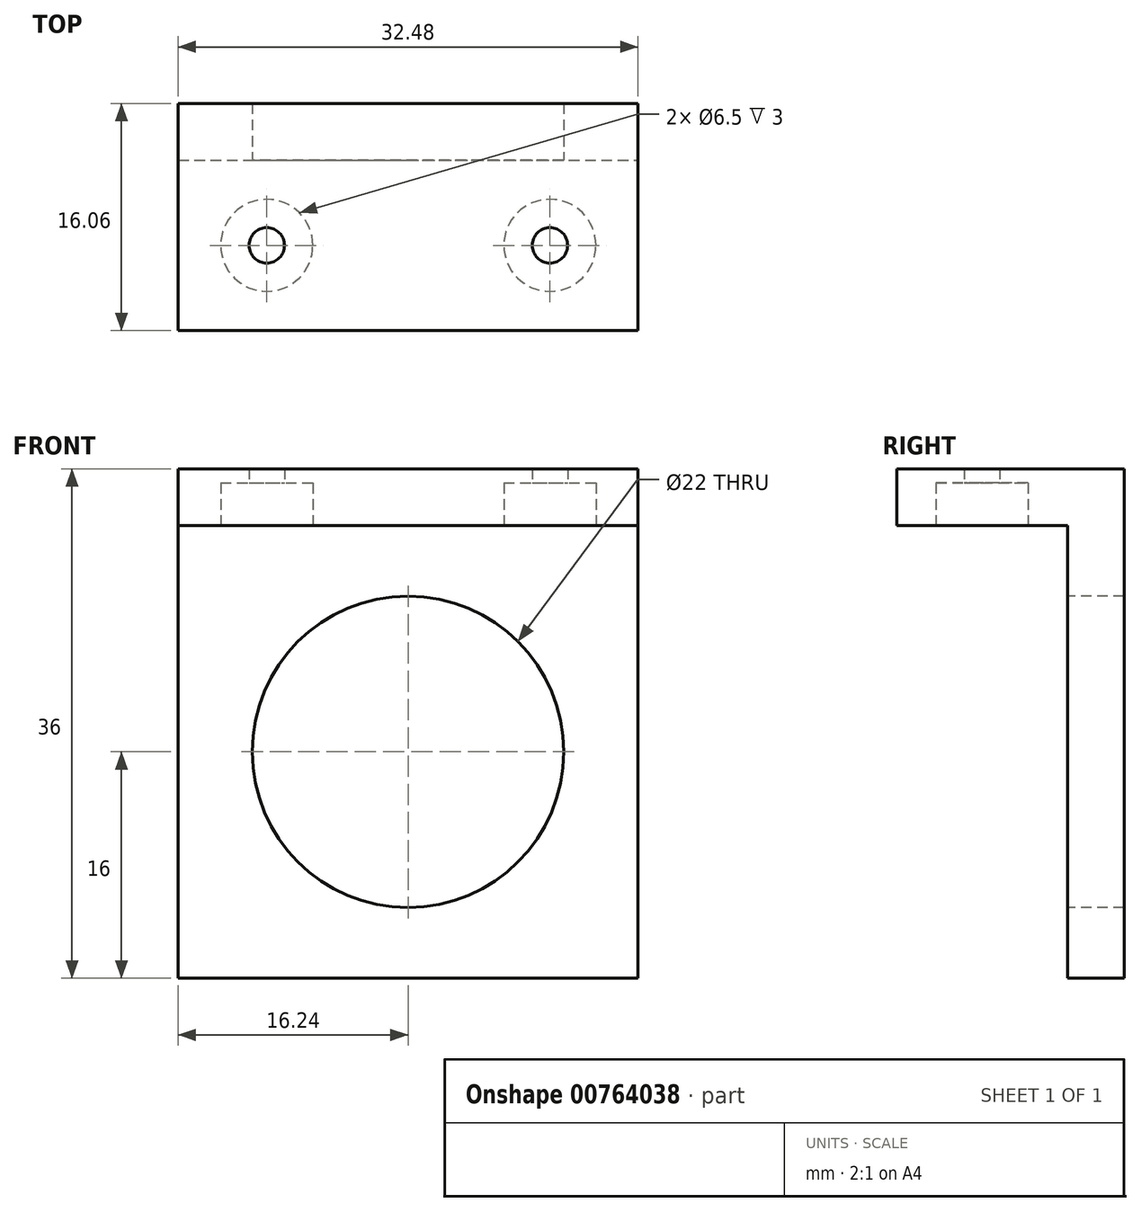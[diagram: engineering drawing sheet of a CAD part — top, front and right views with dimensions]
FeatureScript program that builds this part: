
annotation { "Feature Type Name" : "Feature", "Feature Type Description" : "" }
export const myFeature = defineFeature(function(context is Context, id is Id, definition is map)
    precondition{}
    {
        {
            var Q0;
            Q0=qCreatedBy(makeId("Top.planeOp"),FACE);
            var sketch = newSketch(context, id + "F0", { "sketchPlane" : qUnion([Q0])});
            skLineSegment(sketch, "E0.bottom", {"start": v(-16.24, 6.03) * mm, "end": v(16.24, 6.03) * mm});
            skLineSegment(sketch, "E0.top", {"start": v(-16.24, -6.03) * mm, "end": v(16.24, -6.03) * mm});
            skLineSegment(sketch, "E0.left", {"start": v(-16.24, 6.03) * mm, "end": v(-16.24, -6.03) * mm});
            skLineSegment(sketch, "E0.right", {"start": v(16.24, 6.03) * mm, "end": v(16.24, -6.03) * mm});
            skPoint(sketch, "E0.middle", {"position": v(0, 0) * mm});
            skPoint(sketch, "E1", {"position": v(-9.98, 0) * mm});
            skPoint(sketch, "E2", {"position": v(10.02, 0) * mm});
            skSolve(sketch);
        }
        {
            var Q0;
            Q0=makeQuery(id+"F0.imprint","IMPRINT",FACE,{"disambiguationData":[TD([[makeQuery(id+"F0.imprint","IMPRINT",EDGE,{"derivedFrom":sQuery(id+"F0.wireOp",EDGE,"E0.bottom")}),-1.0]])]});
            extrude(context, id + "F1", {"entities" : qUnion([Q0]), "depth" : 4 * mm, "offsetDistance" : 25 * mm});
        }
        {
            var Q0;
            Q0=sQuery(id+"F0.wireOp",VERTEX,"E2");
            var Q1;
            Q1=sQuery(id+"F0.wireOp",VERTEX,"E1");
            var Q2;
            Q2=makeQuery(id+"F1.opExtrude","SWEPT_BODY",BODY,{"disambiguationData":[OSD([sQuery(id+"F0.wireOp",EDGE,"E0.bottom"),sQuery(id+"F0.wireOp",EDGE,"E0.top"),sQuery(id+"F0.wireOp",EDGE,"E0.left"),sQuery(id+"F0.wireOp",EDGE,"E0.right")])]});
            hole(context, id + "F2", {"style" : HoleStyle.C_BORE, "endStyle" : HoleEndStyle.BLIND, "oppositeDirection" : true, "standardTappedOrClearance" : lookupTablePath({ "standard" : "ISO", "engagement" : "75%", "pitch" : "0.5 mm", "size" : "M3", "type" : "Tapped" }), "standardBlindInLast" : lookupTablePath({ "standard" : "ISO", "engagement" : "75%", "pitch" : "0.5 mm", "size" : "M3", "type" : "Tapped" }), "holeDiameter" : 2.5 * mm, "cBoreDiameter" : 6.5 * mm, "cBoreDepth" : 3 * mm, "majorDiameter" : 3 * mm, "showTappedDepth" : true, "holeDepth" : 13.5 * mm, "isTappedThrough" : true, "tappedDepth" : 12 * mm, "tapClearance" : 3, "locations" : qUnion([Q0, Q1]), "scope" : qUnion([Q2])});
        }
        {
            var Q0;
            Q0=makeQuery(id+"F1.opExtrude","SWEPT_FACE",FACE,{"disambiguationData":[OSD([sQuery(id+"F0.wireOp",EDGE,"E0.bottom")])]});
            var sketch = newSketch(context, id + "F3", { "sketchPlane" : qUnion([Q0])});
            skLineSegment(sketch, "E3.bottom", {"start": v(-16.24, 4) * mm, "end": v(16.24, 4) * mm});
            skLineSegment(sketch, "E3.top", {"start": v(-16.24, -32) * mm, "end": v(16.24, -32) * mm});
            skLineSegment(sketch, "E3.left", {"start": v(-16.24, 4) * mm, "end": v(-16.24, -32) * mm});
            skLineSegment(sketch, "E3.right", {"start": v(16.24, 4) * mm, "end": v(16.24, -32) * mm});
            skPoint(sketch, "E4", {"position": v(0, -16) * mm});
            skCircle(sketch, "E5", {"center": v(0, -16) * mm, "radius": 11 * mm});
            skSolve(sketch);
        }
        {
            var Q0;
            {var subQ0=sQuery(id+"F3.wireOp",EDGE,"E3.bottom");Q0=makeQuery(id+"F3.imprint","IMPRINT",FACE,{"disambiguationData":[TD([[makeQuery(id+"F3.imprint","IMPRINT",EDGE,{"derivedFrom":subQ0}),1.0]])]});}
            var Q1;
            {var subQ2=sQuery(id+"F3.wireOp",EDGE,"E3.top");Q1=makeQuery(id+"F3.imprint","IMPRINT",FACE,{"disambiguationData":[TD([[makeQuery(id+"F3.imprint","IMPRINT",EDGE,{"derivedFrom":subQ2}),1.0]])]});}
            extrude(context, id + "F4", {"entities" : qUnion([Q0, Q1]), "operationType" : NewBodyOperationType.ADD, "depth" : 4 * mm, "offsetDistance" : 25 * mm});
        }
    });
